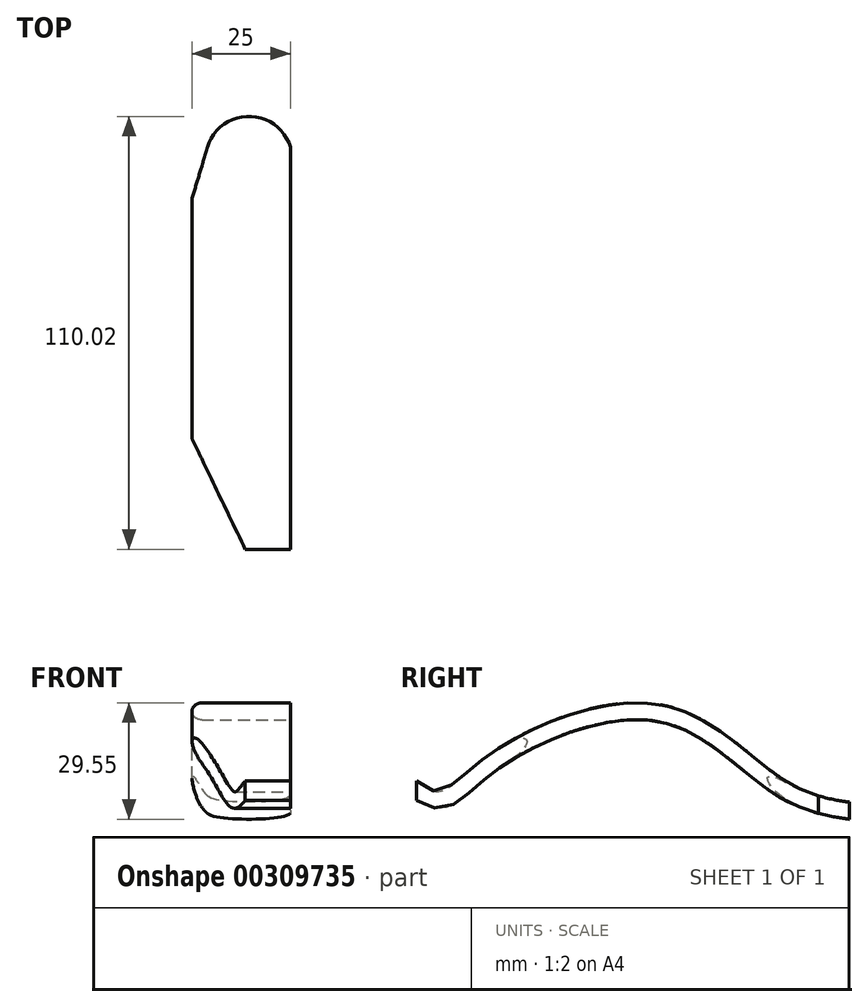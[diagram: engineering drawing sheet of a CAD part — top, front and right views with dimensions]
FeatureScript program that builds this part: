
annotation { "Feature Type Name" : "Feature", "Feature Type Description" : "" }
export const myFeature = defineFeature(function(context is Context, id is Id, definition is map)
    precondition{}
    {
        {
            var Q0;
            Q0=qCreatedBy(makeId("Front.planeOp"),FACE);
            var sketch = newSketch(context, id + "F0", { "sketchPlane" : qUnion([Q0])});
            skLineSegment(sketch, "E0", {"start": v(-22.5, 2.5) * mm, "end": v(22.5, 2.5) * mm});
            skLineSegment(sketch, "E1", {"start": v(22.5, -2.5) * mm, "end": v(-22.5, -2.5) * mm});
            skArc(sketch, "E2", {"start": v(-22.5, 2.5) * mm, "mid": v(-25, 0) * mm, "end": v(-22.5, -2.5) * mm});
            skArc(sketch, "E3", {"start": v(22.5, -2.5) * mm, "mid": v(25, 0) * mm, "end": v(22.5, 2.5) * mm});
            skLineSegment(sketch, "E4", {"start": v(0, -12.04) * mm, "end": v(0, 13.36) * mm, "construction": true});
            skSolve(sketch);
        }
        {
            var Q0;
            Q0=qCreatedBy(makeId("Right.planeOp"),FACE);
            var sketch = newSketch(context, id + "F1", { "sketchPlane" : qUnion([Q0])});
            skFitSpline(sketch, "E5", {"points": [v(0, 0) * mm, v(6.45, -2.16) * mm, v(20.15, 7.66) * mm, v(62.77, 19.46) * mm, v(93.75, 0) * mm, v(117.45, -5.78) * mm], "startDerivative": vector(59.47, -35.45) * mm, "endDerivative": vector(118.37, -9.56) * mm});
            skSolve(sketch);
        }
        {
            var Q0;
            Q0 = qSketchRegion(id + "F0", true);
            var Q1;
            Q1 = qConstructionFilter(qBodyType(qCreatedBy(id + "F1" ,EDGE), BodyType.WIRE), ConstructionObject.NO);
            sweep(context, id + "F2", {"profiles" : qUnion([Q0]), "path" : qUnion([Q1])});
        }
        {
            var Q0;
            Q0=qCreatedBy(makeId("Top.planeOp"),FACE);
            var sketch = newSketch(context, id + "F3", { "sketchPlane" : qUnion([Q0])});
            skLineSegment(sketch, "E6", {"start": v(0, 0) * mm, "end": v(-11.47, 0) * mm});
            skFitSpline(sketch, "E7", {"points": [v(-25, 0) * mm, v(-25, 39.15) * mm, v(-25, 78.3) * mm, v(-25, 117.45) * mm]});
            skLineSegment(sketch, "E8", {"start": v(-11.47, 0) * mm, "end": v(-25, 28.13) * mm});
            skLineSegment(sketch, "E9", {"start": v(-25, 89.09) * mm, "end": v(-21.07, 102.18) * mm});
            skLineSegment(sketch, "E10", {"start": v(0, 102.18) * mm, "end": v(0, 0) * mm});
            skArc(sketch, "E11", {"start": v(0, 102.18) * mm, "mid": v(-10.54, 110.02) * mm, "end": v(-21.07, 102.18) * mm});
            skSolve(sketch);
        }
        {
            var Q0;
            Q0 = qSketchRegion(id + "F3", true);
            extrude(context, id + "F4", {"entities" : qUnion([Q0]), "operationType" : NewBodyOperationType.INTERSECT, "endBound" : BoundingType.SYMMETRIC, "oppositeDirection" : true, "depth" : 100 * mm});
        }
    });
